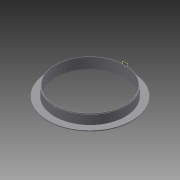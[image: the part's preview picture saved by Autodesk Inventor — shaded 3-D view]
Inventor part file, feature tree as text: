
AUTODESK INVENTOR PART (.ipt)
format: ipt  version: 2015 (Build 190159000, 159)  size: 122,880 bytes
history: native  units: in
note: dims shown in document units (in); Inventor stores cm internally (conversion verified against a paired STEP export)
features: sketch x2, revolve x1, plane x1, hole x1
ambient origin geometry x8: Origin, YZ Plane, XZ Plane, XY Plane, X Axis, Y Axis, Z Axis, Center Point
bodies: Solid1 (feature_tree)
feature tree (5):
  revolve  "Revolution1"  Angle=90.0deg
  plane  "Work Plane1"
  hole  "Hole1"  [1 undecoded]
  sketch  "Sketch1"  dims[d0=1.25in d1=0.125in d2=1.125in d3=4.375in d4=0.125in d5=5.75in d6=0.125in d7=0.5in d8=1.625in d9=0.125in d10=90.0deg]
  sketch  "Sketch2"  dims[d11=0.275in d12=0.75in d13=0.375in d14=0.25in d15=0.5635in d16=1.0in d17=0.8108in]
note: 1 required parameter value undecoded (feature->parameter linkage not recoverable at this tier; creation-order binding heuristic only, values carry confidence <= 0.55)
